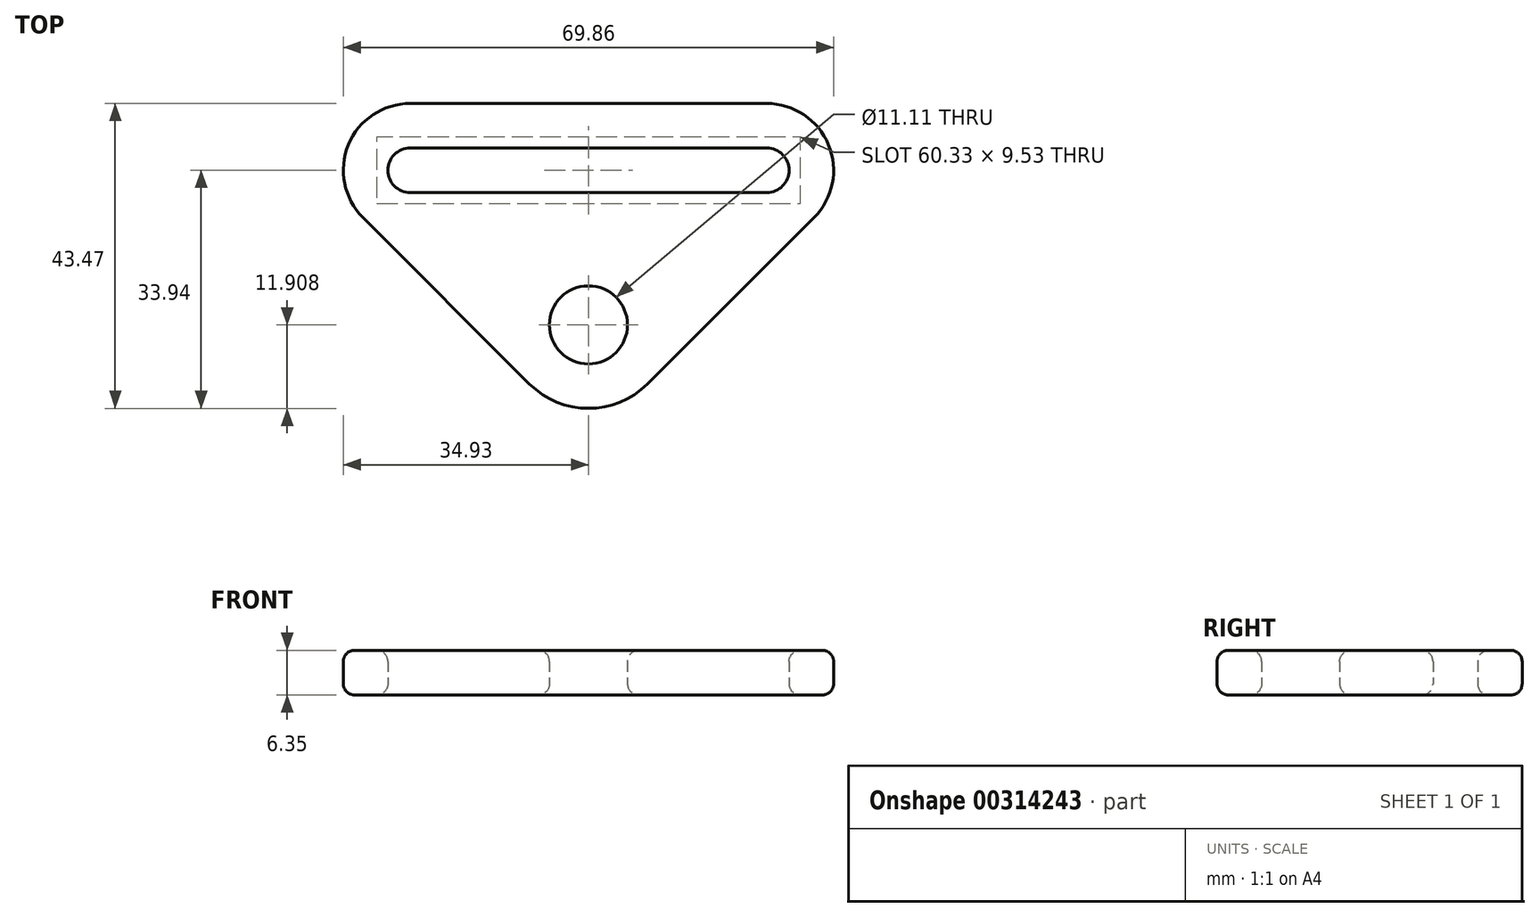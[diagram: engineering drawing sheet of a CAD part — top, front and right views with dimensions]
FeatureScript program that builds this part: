
annotation { "Feature Type Name" : "Feature", "Feature Type Description" : "" }
export const myFeature = defineFeature(function(context is Context, id is Id, definition is map)
    precondition{}
    {
        {
            var Q0;
            Q0=qCreatedBy(makeId("Top.planeOp"),FACE);
            var sketch = newSketch(context, id + "F0", { "sketchPlane" : qUnion([Q0])});
            skLineSegment(sketch, "E0.bottom", {"start": v(-25.4, 3.18) * mm, "end": v(25.4, 3.18) * mm});
            skLineSegment(sketch, "E0.top", {"start": v(-25.4, -3.17) * mm, "end": v(25.4, -3.17) * mm});
            skLineSegment(sketch, "E0.left", {"start": v(-28.58, 0) * mm, "end": v(-28.58, 0) * mm});
            skLineSegment(sketch, "E0.right", {"start": v(28.58, 0) * mm, "end": v(28.58, 0) * mm});
            skPoint(sketch, "E0.middle", {"position": v(0, 0) * mm});
            skPoint(sketch, "E1.visualSharp", {"position": v(-28.58, 3.18) * mm});
            skArc(sketch, "E1.filletArc", {"start": v(-25.4, 3.18) * mm, "mid": v(-27.65, 2.25) * mm, "end": v(-28.57, 0) * mm});
            skPoint(sketch, "E2.visualSharp", {"position": v(-28.58, -3.17) * mm});
            skArc(sketch, "E2.filletArc", {"start": v(-28.57, 0) * mm, "mid": v(-27.65, -2.25) * mm, "end": v(-25.4, -3.17) * mm});
            skPoint(sketch, "E3.visualSharp", {"position": v(28.58, 3.18) * mm});
            skArc(sketch, "E3.filletArc", {"start": v(28.58, 0) * mm, "mid": v(27.65, 2.25) * mm, "end": v(25.4, 3.17) * mm});
            skPoint(sketch, "E4.visualSharp", {"position": v(28.58, -3.17) * mm});
            skArc(sketch, "E4.filletArc", {"start": v(25.4, -3.18) * mm, "mid": v(27.65, -2.25) * mm, "end": v(28.58, 0) * mm});
            skArc(sketch, "E5", {"start": v(-25.4, 9.53) * mm, "mid": v(-34.2, 3.65) * mm, "end": v(-32.14, -6.74) * mm});
            skArc(sketch, "E6", {"start": v(32.14, -6.74) * mm, "mid": v(34.2, 3.65) * mm, "end": v(25.4, 9.53) * mm});
            skLineSegment(sketch, "E7", {"start": v(-25.4, 9.53) * mm, "end": v(25.4, 9.52) * mm});
            skCircle(sketch, "E8", {"center": v(0, -22.03) * mm, "radius": 5.56 * mm});
            skArc(sketch, "E9", {"start": v(-8.42, -30.45) * mm, "mid": v(0, -33.94) * mm, "end": v(8.42, -30.45) * mm});
            skLineSegment(sketch, "E10", {"start": v(-32.14, -6.74) * mm, "end": v(-8.42, -30.45) * mm});
            skLineSegment(sketch, "E11", {"start": v(32.14, -6.74) * mm, "end": v(8.42, -30.45) * mm});
            skCircle(sketch, "E12", {"center": v(0, -22.03) * mm, "radius": 14.29 * mm, "construction": true});
            skSolve(sketch);
        }
        {
            var Q0;
            Q0 = qSketchRegion(id + "F0", true);
            extrude(context, id + "F1", {"entities" : qUnion([Q0]), "depth" : 6.35 * mm});
        }
        {
            var Q0;
            Q0=makeQuery(id+"F1.opExtrude","CAP_FACE",FACE,{"disambiguationData":[OSD([sQuery(id+"F0.wireOp",EDGE,"E0.bottom"),sQuery(id+"F0.wireOp",EDGE,"E0.top"),sQuery(id+"F0.wireOp",EDGE,"E1.filletArc"),sQuery(id+"F0.wireOp",EDGE,"E2.filletArc"),sQuery(id+"F0.wireOp",EDGE,"E3.filletArc"),sQuery(id+"F0.wireOp",EDGE,"E4.filletArc"),sQuery(id+"F0.wireOp",EDGE,"E5"),sQuery(id+"F0.wireOp",EDGE,"E6"),sQuery(id+"F0.wireOp",EDGE,"E7"),sQuery(id+"F0.wireOp",EDGE,"E8"),sQuery(id+"F0.wireOp",EDGE,"E9"),sQuery(id+"F0.wireOp",EDGE,"E10"),sQuery(id+"F0.wireOp",EDGE,"E11")])],"isStart":false});
            fillet(context, id + "F2", {"entities" : qUnion([Q0]), "radius" : 1.59 * mm, "tangentPropagation" : true, "allowEdgeOverflow" : false});
        }
        {
            var Q0;
            Q0=makeQuery(id+"F1.opExtrude","CAP_FACE",FACE,{"disambiguationData":[OSD([sQuery(id+"F0.wireOp",EDGE,"E0.bottom"),sQuery(id+"F0.wireOp",EDGE,"E0.top"),sQuery(id+"F0.wireOp",EDGE,"E1.filletArc"),sQuery(id+"F0.wireOp",EDGE,"E2.filletArc"),sQuery(id+"F0.wireOp",EDGE,"E3.filletArc"),sQuery(id+"F0.wireOp",EDGE,"E4.filletArc"),sQuery(id+"F0.wireOp",EDGE,"E5"),sQuery(id+"F0.wireOp",EDGE,"E6"),sQuery(id+"F0.wireOp",EDGE,"E7"),sQuery(id+"F0.wireOp",EDGE,"E8"),sQuery(id+"F0.wireOp",EDGE,"E9"),sQuery(id+"F0.wireOp",EDGE,"E10"),sQuery(id+"F0.wireOp",EDGE,"E11")])],"isStart":true});
            fillet(context, id + "F3", {"entities" : qUnion([Q0]), "radius" : 1.59 * mm, "tangentPropagation" : true, "allowEdgeOverflow" : false});
        }
    });
